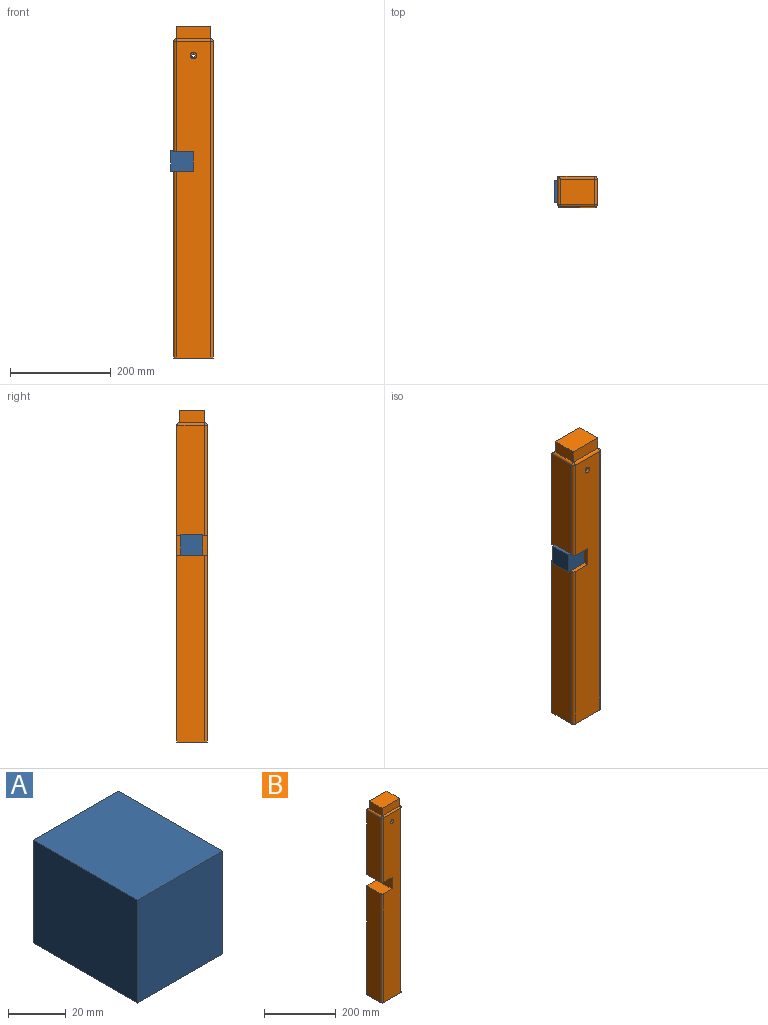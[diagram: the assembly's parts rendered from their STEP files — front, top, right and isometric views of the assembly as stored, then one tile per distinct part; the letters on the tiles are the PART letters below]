
ASSEMBLY  parts=2 mates=1
PART A: 6 faces, bbox 41.8x51.2x43.7 mm
  f0: plane 51.15x43.69mm, normal (1,0,0), area 2234.7mm2, adj f1,f3,f4,f5
  f1: plane 43.69x41.77mm, normal (0,1,0), area 1824.9mm2, adj f0,f2,f4,f5
  f2: plane 51.15x43.69mm, normal (-1,0,0), area 2234.7mm2, adj f1,f3,f4,f5
  f3: plane 43.69x41.77mm, normal (0,-1,0), area 1824.9mm2, adj f0,f2,f4,f5
  f4: plane 51.15x41.77mm, normal (0,0,1), area 2136.6mm2, adj f0,f1,f2,f3
  f5: plane 51.15x41.77mm, normal (0,0,-1), area 2136.6mm2, adj f0,f1,f2,f3
PART B: 28 faces, bbox 78.4x60.7x660.4 mm
  f0: plane 219.51x55.58mm, normal (-1,0,0), area 12200.1mm2, adj f2,f5,f12,f25
  f1: plane 629.92x68.21mm, normal (0,-1,0), area 41504.1mm2, adj f2,f3,f7,f8,f9,f19,f25,f26
  f2: cylinder r=5.08mm len=219.51mm, axis (0,0,1), area 1751.6mm2, adj f0,f1,f10,f25
  f3: cylinder r=5.08mm len=371.27mm, axis (0,0,1), area 2962.6mm2, adj f1,f6,f7,f27
  f4: plane 629.92x50.5mm, normal (1,0,0), area 31809.6mm2, adj f7,f8,f13,f16
  f5: plane 629.92x73.29mm, normal (0,1,0), area 44600.3mm2, adj f0,f6,f7,f14,f16,f17,f25,f26
  f6: plane 371.27x55.58mm, normal (-1,0,0), area 20634.2mm2, adj f3,f5,f7,f27
  f7: plane 78.37x60.66mm, normal (0,0,-1), area 4737mm2, adj f1,f3,f4,f5,f6,f8,f16
  f8: cylinder r=5.08mm len=629.92mm, axis (0,0,-1), area 5026.5mm2, adj f1,f4,f7,f11
  f9: cylinder r=5.08mm len=68.21mm, axis (-1,0,0), area 544.3mm2, adj f1,f10,f11,f22
  f10: sphere r=5.08mm, area 40.5mm2, adj f2,f9,f12
  f11: sphere r=5.08mm, area 40.5mm2, adj f8,f9,f13
  f12: cylinder r=5.08mm len=55.58mm, axis (0,1,0), area 428.8mm2, adj f0,f10,f14,f21
  f13: cylinder r=5.08mm len=50.5mm, axis (0,-1,0), area 403mm2, adj f4,f11,f15,f23
  f14: cylinder r=5.08mm len=73.29mm, axis (1,0,0), area 570.1mm2, adj f5,f12,f15,f20
  f15: sphere r=5.08mm, area 40.5mm2, adj f13,f14,f16
  f16: cylinder r=5.08mm len=629.92mm, axis (0,0,1), area 5026.5mm2, adj f4,f5,f7,f15
  f17: cylinder r=3.17mm len=54.31mm, axis (0,-1,0), area 1083.4mm2, adj f5,f18
  f18: plane 12.7x12.7mm, normal (0,-1,0), area 95mm2, adj f17,f19
  f19: cylinder r=6.35mm len=12.7mm, axis (0,-1,0), area 253.4mm2, adj f1,f18
  f20: plane 68.21x25.4mm, normal (0,1,0), area 1732.5mm2, adj f14,f21,f23,f24
  f21: plane 50.5x25.4mm, normal (-1,0,0), area 1282.6mm2, adj f12,f20,f22,f24
  f22: plane 68.21x25.4mm, normal (0,-1,0), area 1732.5mm2, adj f9,f21,f23,f24
  f23: plane 50.5x25.4mm, normal (1,0,0), area 1282.6mm2, adj f13,f20,f22,f24
  f24: plane 68.21x50.5mm, normal (0,0,1), area 3444.3mm2, adj f20,f21,f22,f23
  f25: plane 60.66x39.18mm, normal (0,0,-1), area 2371.3mm2, adj f0,f1,f2,f5,f26
  f26: plane 60.66x39.14mm, normal (-1,0,0), area 2374mm2, adj f1,f5,f25,f27
  f27: plane 60.66x39.18mm, normal (0,0,1), area 2371.3mm2, adj f1,f3,f5,f6,f26
PLACE A rot(axis=(0.58,0.58,-0.58),120deg) t=(-152.02,-6.54,91.45)mm
PLACE B t=(-132.48,-28.46,-300.71)mm
MATE planar B.f27 <-> A.f0  axis (0,0,1) through (-152.02,-28.39,70.56)mm
